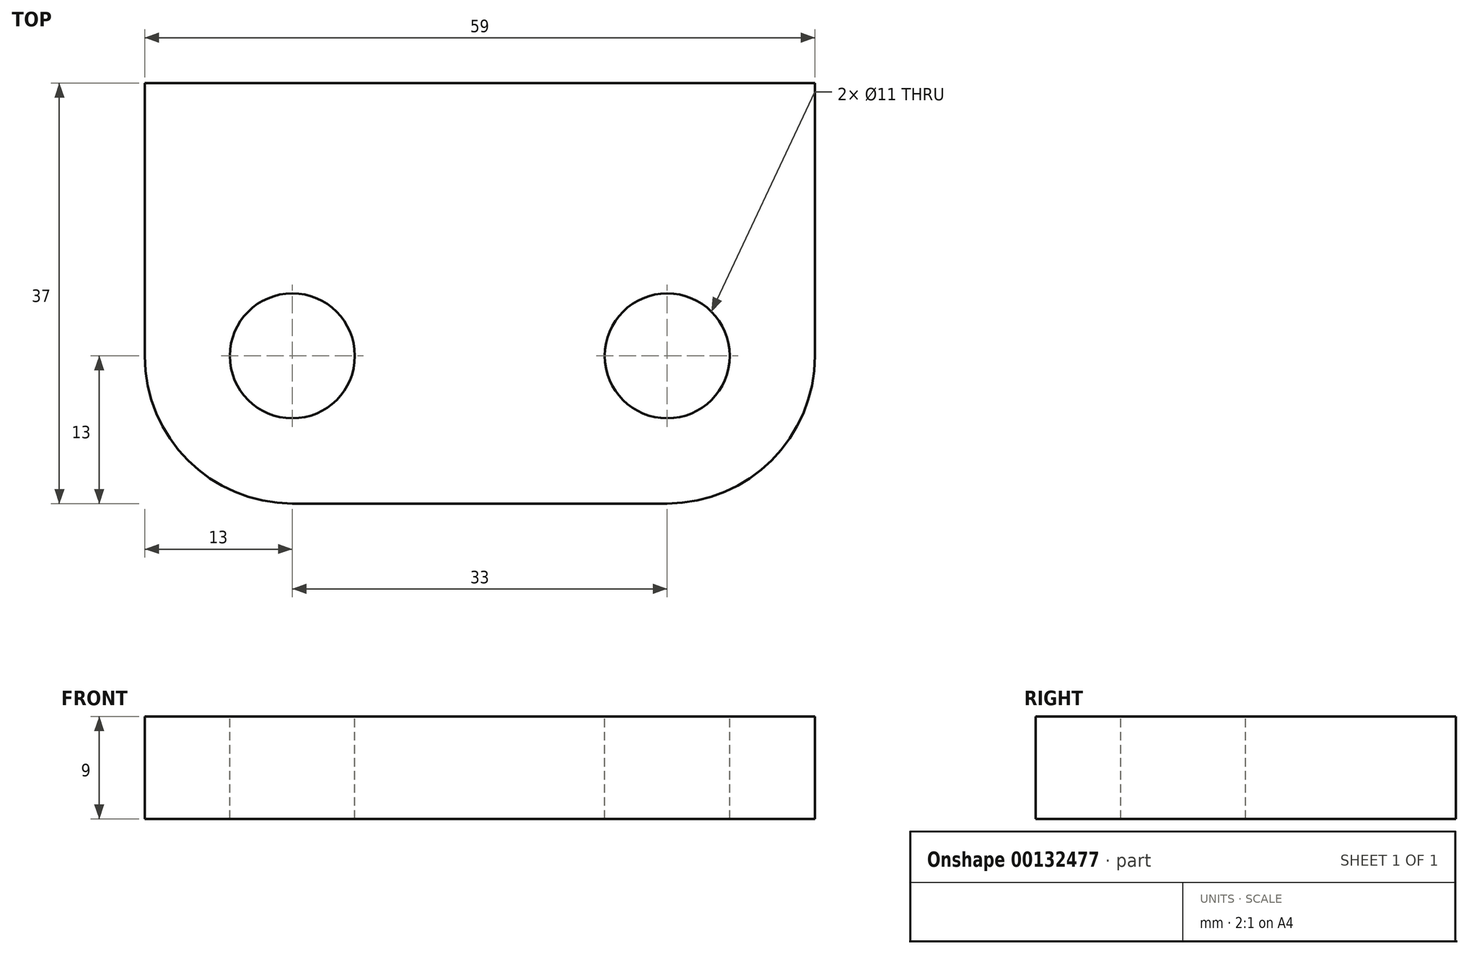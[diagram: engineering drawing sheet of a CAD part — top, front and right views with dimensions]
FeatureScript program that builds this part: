
annotation { "Feature Type Name" : "Feature", "Feature Type Description" : "" }
export const myFeature = defineFeature(function(context is Context, id is Id, definition is map)
    precondition{}
    {
        {
            var Q0;
            Q0=qCreatedBy(makeId("Top.planeOp"),FACE);
            var sketch = newSketch(context, id + "F0", { "sketchPlane" : qUnion([Q0])});
            skLineSegment(sketch, "E0", {"start": v(0, 0) * mm, "end": v(59, 0) * mm});
            skLineSegment(sketch, "E1", {"start": v(0, 0) * mm, "end": v(0, -24) * mm});
            skLineSegment(sketch, "E2", {"start": v(13, -37) * mm, "end": v(46, -37) * mm});
            skPoint(sketch, "E3.visualSharp", {"position": v(0, -37) * mm});
            skArc(sketch, "E3.filletArc", {"start": v(0, -24) * mm, "mid": v(3.8, -33.2) * mm, "end": v(13, -37) * mm});
            skLineSegment(sketch, "E4", {"start": v(59, 0) * mm, "end": v(59, -24) * mm});
            skPoint(sketch, "E5.visualSharp", {"position": v(59, -37) * mm});
            skArc(sketch, "E5.filletArc", {"start": v(46, -37) * mm, "mid": v(55.2, -33.2) * mm, "end": v(59, -24) * mm});
            skCircle(sketch, "E6", {"center": v(13, -24) * mm, "radius": 5.5 * mm});
            skCircle(sketch, "E7", {"center": v(46, -24) * mm, "radius": 5.5 * mm});
            skSolve(sketch);
        }
        {
            var Q0;
            Q0=makeQuery(id+"F0.imprint","IMPRINT",FACE,{"disambiguationData":[TD([[makeQuery(id+"F0.imprint","IMPRINT",EDGE,{"derivedFrom":sQuery(id+"F0.wireOp",EDGE,"E0")}),-1.0]])]});
            extrude(context, id + "F1", {"entities" : qUnion([Q0]), "oppositeDirection" : true, "depth" : 9 * mm});
        }
    });
